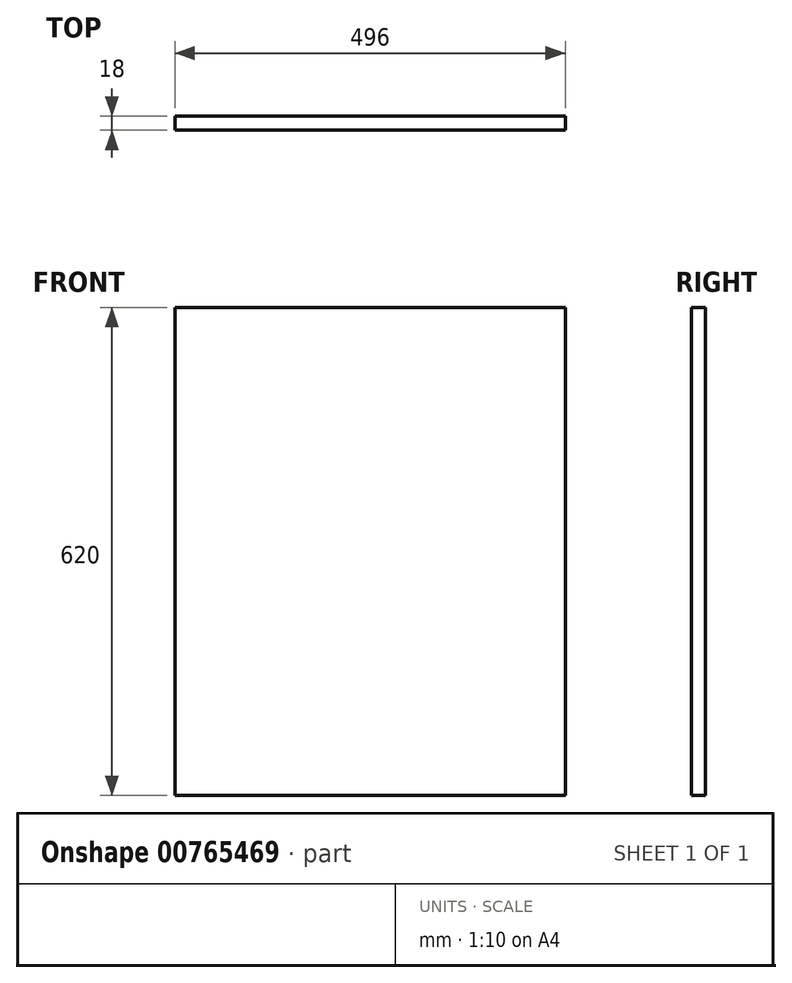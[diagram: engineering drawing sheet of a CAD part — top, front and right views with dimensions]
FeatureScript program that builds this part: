
annotation { "Feature Type Name" : "Feature", "Feature Type Description" : "" }
export const myFeature = defineFeature(function(context is Context, id is Id, definition is map)
    precondition{}
    {
        {
            var Q0;
            Q0=qCreatedBy(makeId("Front.planeOp"),FACE);
            var sketch = newSketch(context, id + "F0", { "sketchPlane" : qUnion([Q0])});
            skLineSegment(sketch, "E0.bottom", {"start": v(-248, -310) * mm, "end": v(248, -310) * mm});
            skLineSegment(sketch, "E0.top", {"start": v(-248, 310) * mm, "end": v(248, 310) * mm});
            skLineSegment(sketch, "E0.left", {"start": v(-248, -310) * mm, "end": v(-248, 310) * mm});
            skLineSegment(sketch, "E0.right", {"start": v(248, -310) * mm, "end": v(248, 310) * mm});
            skPoint(sketch, "E0.middle", {"position": v(0, 0) * mm});
            skSolve(sketch);
        }
        {
            var Q0;
            Q0 = qSketchRegion(id + "F0", true);
            extrude(context, id + "F1", {"entities" : qUnion([Q0]), "depth" : 18 * mm, "offsetDistance" : 25 * mm});
        }
    });
